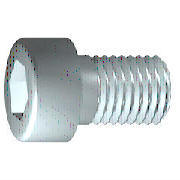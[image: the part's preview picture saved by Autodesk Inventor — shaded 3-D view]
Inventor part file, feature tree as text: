
AUTODESK INVENTOR PART (.ipt)
format: ipt  version: 2019.1 (Build 231200000, 200)  size: 194,048 bytes
history: native  units: mm (DEFAULTED — no unit token found)
features: sketch x2, extrude x1, plane x1, fillet x1
ambient origin geometry x7: Origin, YZ Plane, XY Plane, X Axis, Y Axis, Z Axis, Center Point
bodies: Solid1 (feature_tree), Body (feature_tree)
feature tree (5):
  extrude  "Slot"  Depth=3.1751mm
  plane  "Work Plane1"
  fillet  "Fillet2"  Radius=6.35mm
  sketch  "Sketch1"  dims[d1=15.8748mm d2=3.1751mm d3=6.35mm]
  sketch  "Sketch2"  dims[d4=3.048mm d5=60.0deg d6=6.35mm d7=6.35mm d8=5.513926mm d9=9.525mm d10=90.0deg d11=10.0mm d12=0.0mm d13=15.8748mm d14=0.0mm d15=0.75565mm d16=0.75565mm d17=0.635mm d19=0.0mm d26=19.05mm d27=45.0deg d28=0.0mm d29=0.0mm d30=0.1778mm]
